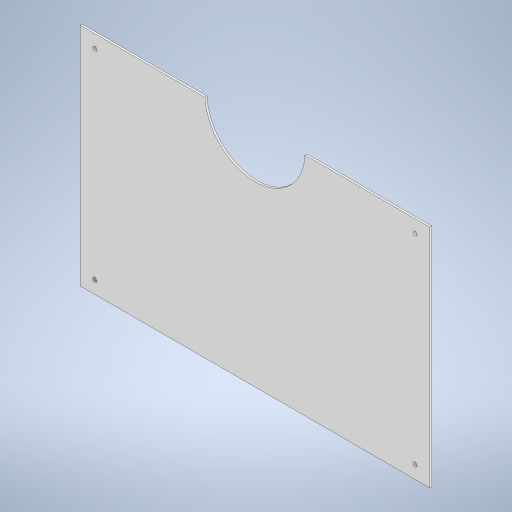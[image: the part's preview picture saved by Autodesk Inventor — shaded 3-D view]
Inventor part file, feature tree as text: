
AUTODESK INVENTOR PART (.ipt)
format: ipt  version: 2023 (Build 270158000, 158)  size: 227,328 bytes
history: native  units: mm
features: sketch x2, extrude x1, hole x1
ambient origin geometry x8: Origin, YZ Plane, XZ Plane, XY Plane, X Axis, Y Axis, Z Axis, Center Point
bodies: Solid1 (feature_tree)
feature tree (4):
  extrude  "Extrusion1"  Depth=350.0mm
  hole  "Hole1"  [1 undecoded]
  sketch  "Sketch1"  dims[d0=542.0mm d1=350.0mm]
  sketch  "Sketch2"  dims[d2=3.0mm d3=0.0mm d4=23.0mm d6=6.5mm d7=6.0mm d8=4.0mm d9=2.0mm d10=90.0deg d11=8.0mm d12=20.594885mm d13=20.0mm d14=350.0mm d15=542.0mm d16=20.0mm d18=310.0mm d19=20.0mm d21=496.0mm d24=155.0mm d25=353.0mm]
note: 1 required parameter value undecoded (feature->parameter linkage not recoverable at this tier; creation-order binding heuristic only, values carry confidence <= 0.55)
